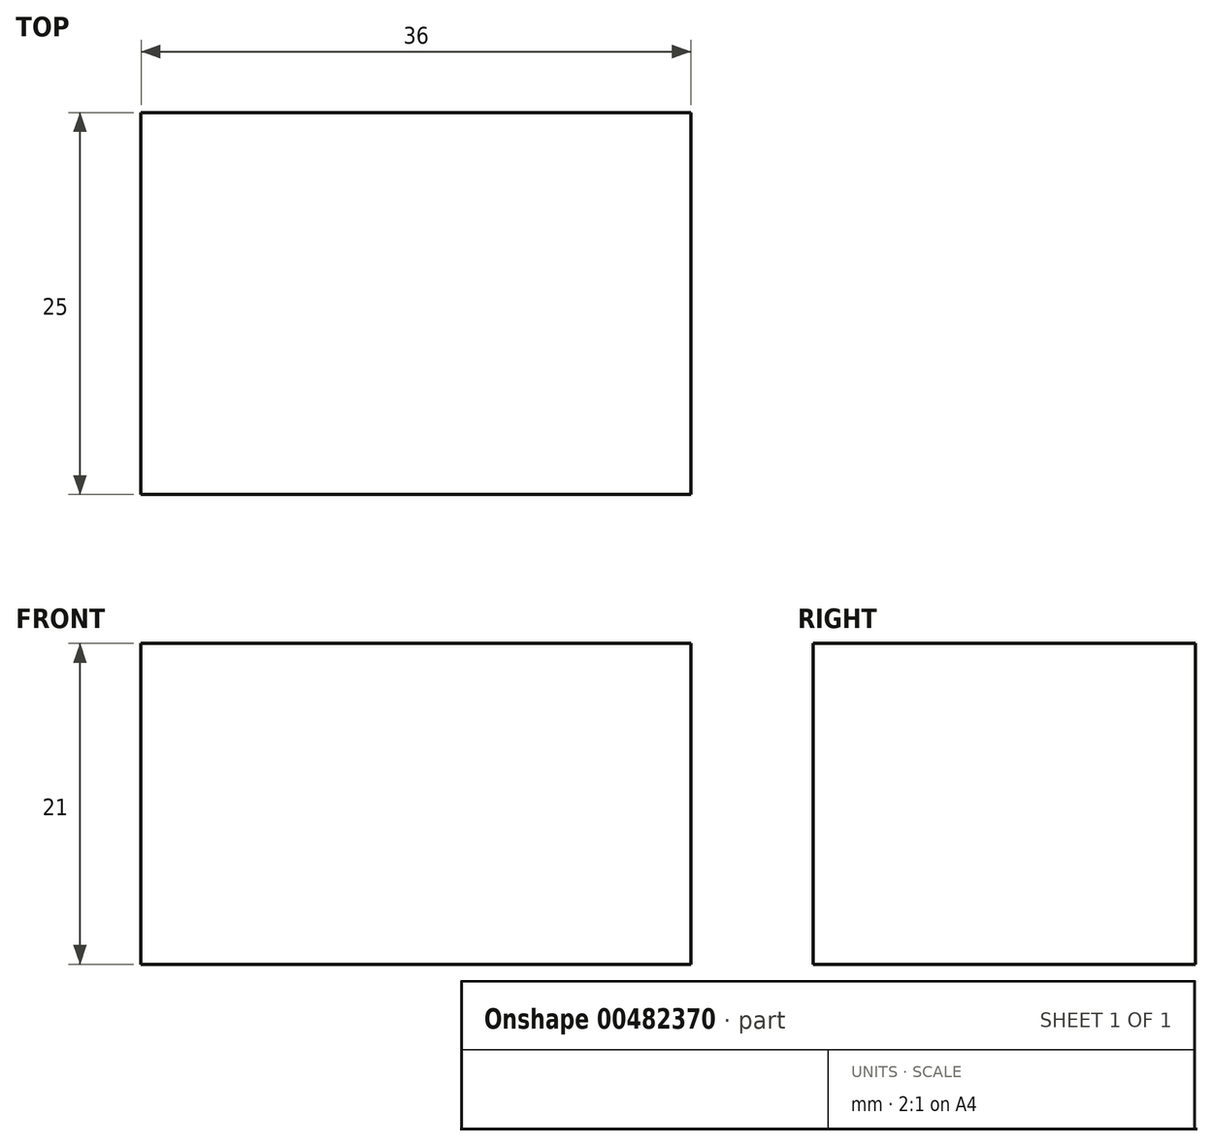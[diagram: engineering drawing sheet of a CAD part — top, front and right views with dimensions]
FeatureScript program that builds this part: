
annotation { "Feature Type Name" : "Feature", "Feature Type Description" : "" }
export const myFeature = defineFeature(function(context is Context, id is Id, definition is map)
    precondition{}
    {
        {
            var Q0;
            Q0=qCreatedBy(makeId("Front.planeOp"),FACE);
            var sketch = newSketch(context, id + "F0", { "sketchPlane" : qUnion([Q0])});
            skLineSegment(sketch, "E0.bottom", {"start": v(-45.68, 26.43) * mm, "end": v(-9.68, 26.43) * mm});
            skLineSegment(sketch, "E0.top", {"start": v(-45.68, 5.43) * mm, "end": v(-9.68, 5.43) * mm});
            skLineSegment(sketch, "E0.left", {"start": v(-45.68, 26.43) * mm, "end": v(-45.68, 5.43) * mm});
            skLineSegment(sketch, "E0.right", {"start": v(-9.68, 26.43) * mm, "end": v(-9.68, 5.43) * mm});
            skSolve(sketch);
        }
        {
            var Q0;
            {var subQ0=sQuery(id+"F0.wireOp",EDGE,"E0.left");Q0=makeQuery(id+"F0.imprint","IMPRINT",FACE,{"disambiguationData":[TD([[makeQuery(id+"F0.imprint","IMPRINT",EDGE,{"derivedFrom":subQ0}),1.0]])]});}
            var Q1;
            {var subQ0=sQuery(id+"F0.wireOp",EDGE,"E0.right");Q1=makeQuery(id+"F0.imprint","IMPRINT",FACE,{"disambiguationData":[TD([[makeQuery(id+"F0.imprint","IMPRINT",EDGE,{"derivedFrom":subQ0}),-1.0]])]});}
            extrude(context, id + "F1", {"entities" : qUnion([Q0, Q1]), "endBound" : BoundingType.SYMMETRIC, "depth" : 25 * mm});
        }
    });
